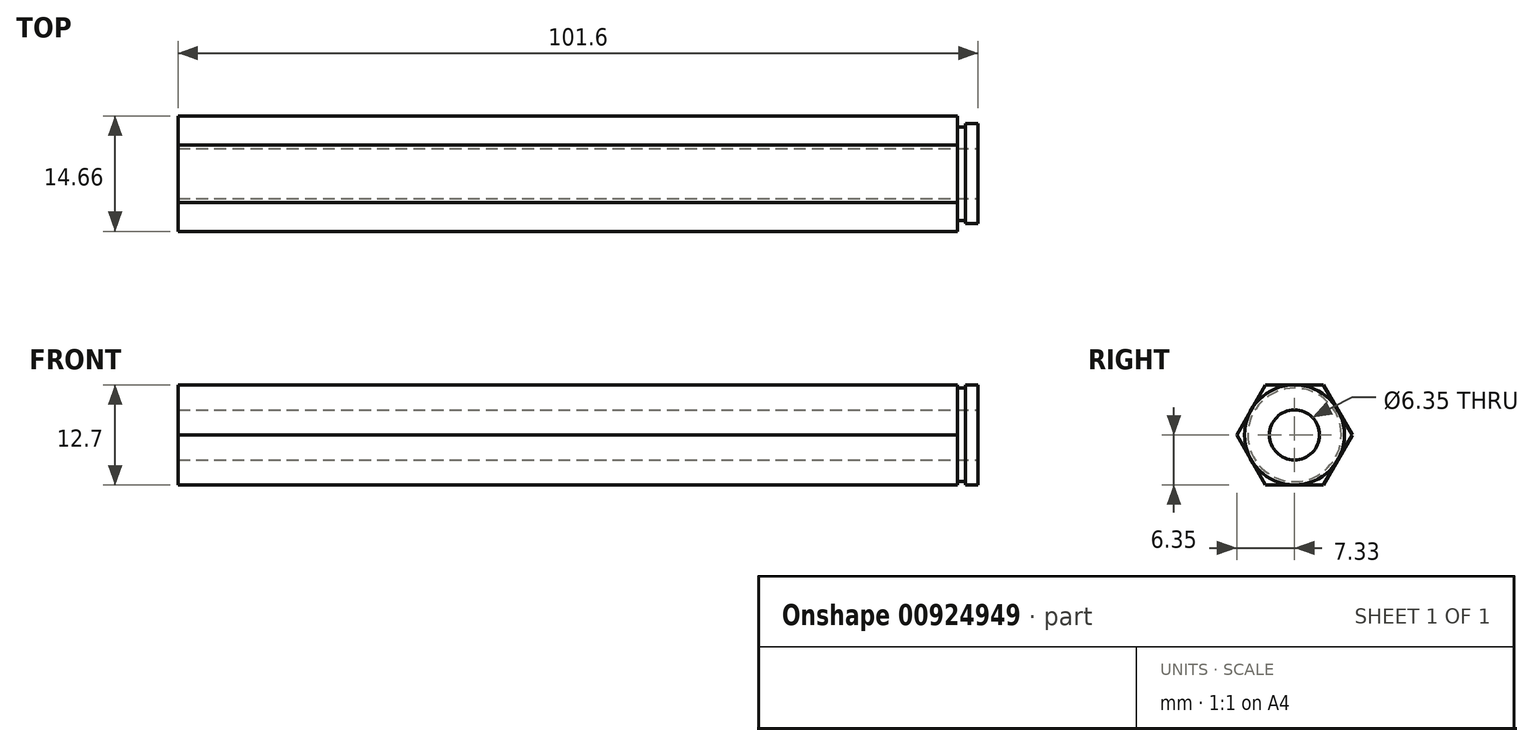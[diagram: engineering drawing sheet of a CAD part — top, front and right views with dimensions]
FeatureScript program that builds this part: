
annotation { "Feature Type Name" : "Feature", "Feature Type Description" : "" }
export const myFeature = defineFeature(function(context is Context, id is Id, definition is map)
    precondition{}
    {
        {
            var Q0;
            Q0=qCreatedBy(makeId("Right.planeOp"),FACE);
            var sketch = newSketch(context, id + "F0", { "sketchPlane" : qUnion([Q0])});
            skCircle(sketch, "E0.cCircle", {"center": v(0, 0) * mm, "radius": 6.35 * mm, "construction": true});
            skLineSegment(sketch, "E0.0", {"start": v(-3.67, 6.35) * mm, "end": v(3.67, 6.35) * mm});
            skLineSegment(sketch, "E0.1", {"start": v(3.67, 6.35) * mm, "end": v(7.33, 0) * mm});
            skLineSegment(sketch, "E0.2", {"start": v(7.33, 0) * mm, "end": v(3.67, -6.35) * mm});
            skLineSegment(sketch, "E0.3", {"start": v(3.67, -6.35) * mm, "end": v(-3.67, -6.35) * mm});
            skLineSegment(sketch, "E0.4", {"start": v(-3.67, -6.35) * mm, "end": v(-7.33, 0) * mm});
            skLineSegment(sketch, "E0.5", {"start": v(-7.33, 0) * mm, "end": v(-3.67, 6.35) * mm});
            skPoint(sketch, "E0.0.midPoint", {"position": v(0, 6.35) * mm});
            skSolve(sketch);
        }
        {
            var Q0;
            Q0 = qSketchRegion(id + "F0", true);
            extrude(context, id + "F1", {"entities" : qUnion([Q0]), "depth" : 101.6 * mm, "offsetDistance" : 25.4 * mm});
        }
        {
            var Q0;
            Q0=qCreatedBy(makeId("Top.planeOp"),FACE);
            var sketch = newSketch(context, id + "F2", { "sketchPlane" : qUnion([Q0])});
            skLineSegment(sketch, "E1", {"start": v(101.6, 6.35) * mm, "end": v(100.01, 6.35) * mm});
            skLineSegment(sketch, "E2", {"start": v(100.01, 6.35) * mm, "end": v(100.01, 5.94) * mm});
            skLineSegment(sketch, "E3", {"start": v(100.01, 5.94) * mm, "end": v(99.02, 5.94) * mm});
            skLineSegment(sketch, "E4", {"start": v(99.02, 5.94) * mm, "end": v(99.02, 7.33) * mm});
            skLineSegment(sketch, "E5", {"start": v(0, 0) * mm, "end": v(101.6, 0) * mm, "construction": true});
            skLineSegment(sketch, "E6", {"start": v(101.6, 6.35) * mm, "end": v(101.6, 7.33) * mm});
            skLineSegment(sketch, "E7", {"start": v(101.6, 7.33) * mm, "end": v(99.02, 7.33) * mm});
            skSolve(sketch);
        }
        {
            var Q0;
            Q0 = qSketchRegion(id + "F2", true);
            var Q1;
            Q1=sQuery(id+"F2.wireOp",EDGE,"E5");
            revolve(context, id + "F3", {"operationType" : NewBodyOperationType.REMOVE, "surfaceOperationType" : NewSurfaceOperationType.NEW, "entities" : qUnion([Q0]), "axis" : qUnion([Q1]), "revolveType" : RevolveType.FULL, "oppositeDirection" : true});
        }
        {
            var Q0;
            Q0=makeQuery(id+"F1.opExtrude","CAP_FACE",FACE,{"disambiguationData":[OSD([sQuery(id+"F0.wireOp",EDGE,"E0.0"),sQuery(id+"F0.wireOp",EDGE,"E0.1"),sQuery(id+"F0.wireOp",EDGE,"E0.2"),sQuery(id+"F0.wireOp",EDGE,"E0.3"),sQuery(id+"F0.wireOp",EDGE,"E0.4"),sQuery(id+"F0.wireOp",EDGE,"E0.5")])],"isStart":false});
            var sketch = newSketch(context, id + "F4", { "sketchPlane" : qUnion([Q0])});
            skCircle(sketch, "E8", {"center": v(0, 0) * mm, "radius": 3.18 * mm});
            skSolve(sketch);
        }
        {
            var Q0;
            Q0 = qSketchRegion(id + "F4", true);
            extrude(context, id + "F5", {"entities" : qUnion([Q0]), "operationType" : NewBodyOperationType.REMOVE, "endBound" : BoundingType.THROUGH_ALL, "oppositeDirection" : true, "depth" : 25.4 * mm, "offsetDistance" : 25.4 * mm});
        }
    });
